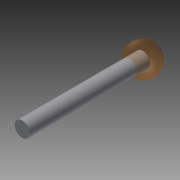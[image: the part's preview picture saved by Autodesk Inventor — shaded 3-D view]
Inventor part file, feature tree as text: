
AUTODESK INVENTOR PART (.ipt)
format: ipt  version: 2016 (Build 200138000, 138)  size: 104,448 bytes
history: native  units: in
note: dims shown in document units (in); Inventor stores cm internally (conversion verified against a paired STEP export)
features: sketch x2, extrude x1, other x1, revolve x1
ambient origin geometry x8: Origin, YZ Plane, XZ Plane, XY Plane, X Axis, Y Axis, Z Axis, Center Point
bodies: Solid1 (feature_tree)
feature tree (5):
  extrude  "Extrusion1"  Depth=0.5in
  sketch  "Sketch1"  dims[d1=90.0deg d2=0.5in]
  other  "Srf1"
  sketch  "Sketch2"  dims[d3=2.5in d4=0.0in]
  revolve  "RevolutionSrf1"  [1 undecoded]
note: 1 required parameter value undecoded (feature->parameter linkage not recoverable at this tier; creation-order binding heuristic only, values carry confidence <= 0.55)
